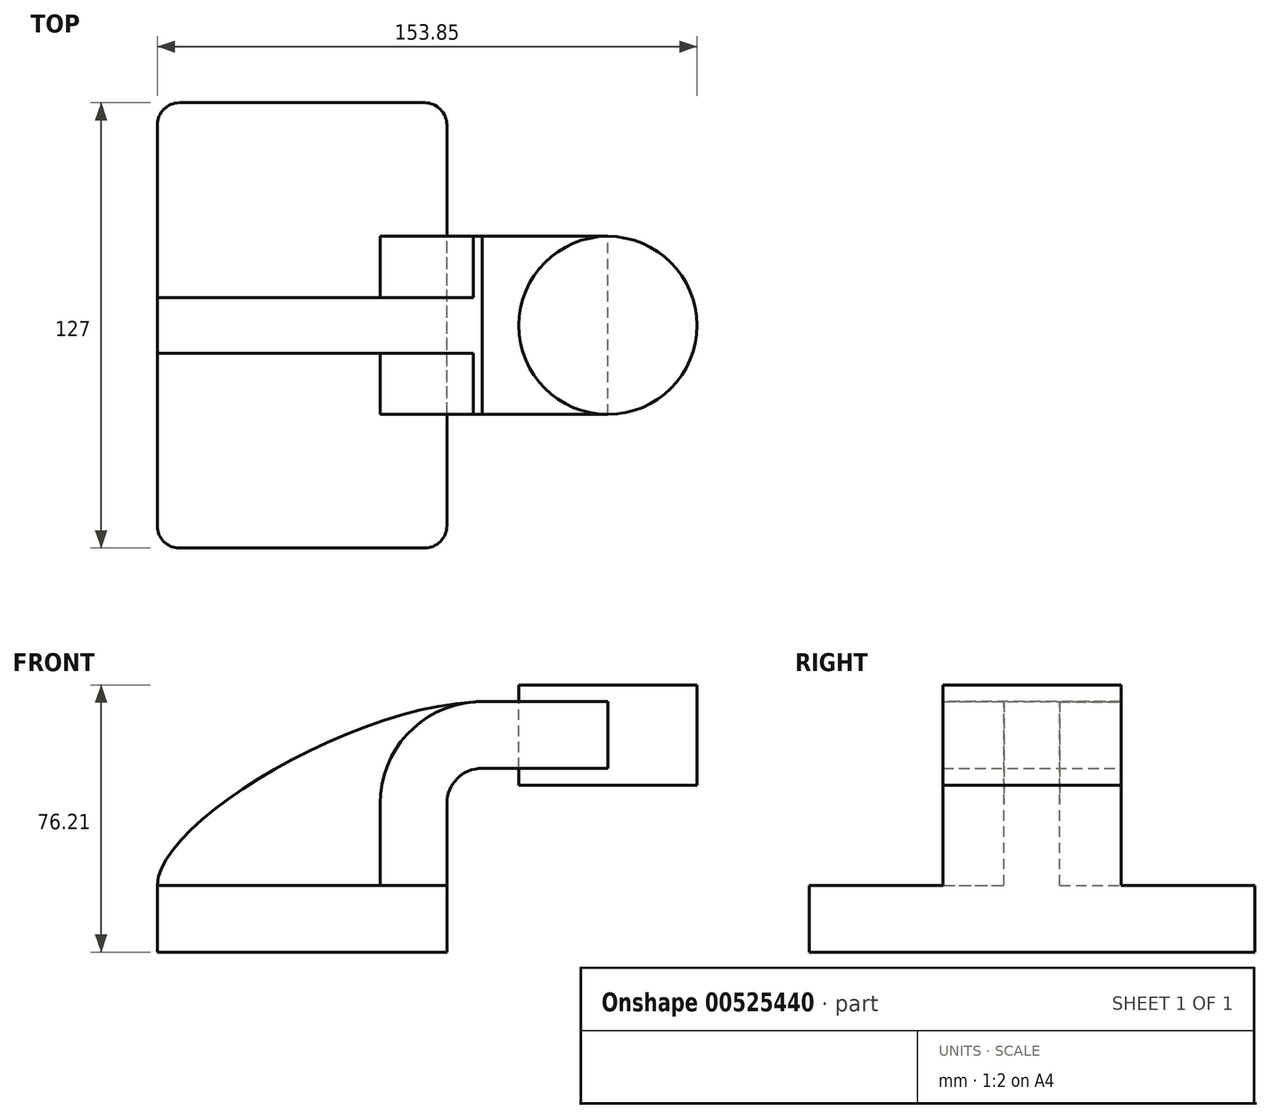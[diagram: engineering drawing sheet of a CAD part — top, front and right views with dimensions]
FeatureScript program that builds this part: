
annotation { "Feature Type Name" : "Feature", "Feature Type Description" : "" }
export const myFeature = defineFeature(function(context is Context, id is Id, definition is map)
    precondition{}
    {
        {
            var Q0;
            Q0=qCreatedBy(makeId("Front.planeOp"),FACE);
            var sketch = newSketch(context, id + "F0", { "sketchPlane" : qUnion([Q0])});
            skLineSegment(sketch, "E0.bottom", {"start": v(-41.28, 9.52) * mm, "end": v(41.27, 9.53) * mm});
            skLineSegment(sketch, "E0.top", {"start": v(-41.28, -9.53) * mm, "end": v(41.28, -9.53) * mm});
            skLineSegment(sketch, "E0.left", {"start": v(-41.28, 9.52) * mm, "end": v(-41.27, -9.53) * mm});
            skLineSegment(sketch, "E0.right", {"start": v(41.28, 9.53) * mm, "end": v(41.28, -9.52) * mm});
            skPoint(sketch, "E0.middle", {"position": v(0, 0) * mm});
            skLineSegment(sketch, "E1.bottom", {"start": v(112.57, 66.68) * mm, "end": v(61.77, 66.68) * mm});
            skLineSegment(sketch, "E1.top", {"start": v(112.57, 38.1) * mm, "end": v(61.77, 38.1) * mm});
            skLineSegment(sketch, "E1.left", {"start": v(112.57, 66.68) * mm, "end": v(112.57, 38.1) * mm});
            skLineSegment(sketch, "E1.right", {"start": v(61.77, 66.67) * mm, "end": v(61.77, 38.1) * mm});
            skPoint(sketch, "E1.middle", {"position": v(87.17, 52.39) * mm});
            skLineSegment(sketch, "E2", {"start": v(41.27, 9.53) * mm, "end": v(41.27, 32.83) * mm});
            skArc(sketch, "E3", {"start": v(41.27, 32.83) * mm, "mid": v(44.22, 39.93) * mm, "end": v(51.32, 42.88) * mm});
            skLineSegment(sketch, "E4", {"start": v(51.32, 42.88) * mm, "end": v(87.17, 42.88) * mm});
            skLineSegment(sketch, "E5.0", {"start": v(51.32, 61.93) * mm, "end": v(87.17, 61.93) * mm});
            skArc(sketch, "E5.1", {"start": v(22.22, 32.83) * mm, "mid": v(30.75, 53.4) * mm, "end": v(51.32, 61.93) * mm});
            skLineSegment(sketch, "E5.2", {"start": v(22.22, 9.53) * mm, "end": v(22.22, 32.83) * mm});
            skLineSegment(sketch, "E6", {"start": v(87.17, 38.1) * mm, "end": v(87.17, 66.68) * mm});
            skFitSpline(sketch, "E7", {"points": [v(-41.28, 9.52) * mm, v(51.32, 61.93) * mm], "startDerivative": vector(0, 52.78) * mm, "endDerivative": vector(111.48, 2.71) * mm});
            skSolve(sketch);
        }
        {
            var Q0;
            Q0=makeQuery(id+"F0.imprint","IMPRINT",FACE,{"disambiguationData":[TD([[makeQuery(id+"F0.imprint","IMPRINT",EDGE,{"derivedFrom":sQuery(id+"F0.wireOp",EDGE,"E0.top")}),1.0]])]});
            extrude(context, id + "F1", {"entities" : qUnion([Q0]), "endBound" : BoundingType.SYMMETRIC, "depth" : 127 * mm, "offsetDistance" : 25.4 * mm});
        }
        {
            var Q0;
            {var subQ1=sQuery(id+"F0.wireOp",EDGE,"E2");Q0=makeQuery(id+"F0.imprint","IMPRINT",FACE,{"disambiguationData":[TD([[makeQuery(id+"F0.imprint","IMPRINT",EDGE,{"derivedFrom":subQ1}),1.0]])]});}
            var Q1;
            {var subQ0=sQuery(id+"F0.wireOp",EDGE,"E5.0");var subQ1=sQuery(id+"F0.wireOp",EDGE,"E1.right");var subQ2=makeQuery(id+"F0.imprint","INTERSECT",VERTEX,{"derivedFrom":[subQ1,subQ0]});Q1=makeQuery(id+"F0.imprint","IMPRINT",FACE,{"disambiguationData":[TD([[makeQuery(id+"F0.imprint","IMPRINT",EDGE,{"disambiguationData":[TD([[subQ2,-1.0]])],"derivedFrom":subQ1}),1.0]])]});}
            extrude(context, id + "F2", {"entities" : qUnion([Q0, Q1]), "operationType" : NewBodyOperationType.ADD, "endBound" : BoundingType.SYMMETRIC, "depth" : 50.8 * mm, "offsetDistance" : 25.4 * mm});
        }
        {
            var Q0;
            {var subQ3=sQuery(id+"F0.wireOp",EDGE,"E5.2");Q0=makeQuery(id+"F0.imprint","IMPRINT",FACE,{"disambiguationData":[TD([[makeQuery(id+"F0.imprint","IMPRINT",EDGE,{"derivedFrom":subQ3}),1.0]])]});}
            extrude(context, id + "F3", {"entities" : qUnion([Q0]), "operationType" : NewBodyOperationType.ADD, "endBound" : BoundingType.SYMMETRIC, "depth" : 15.88 * mm, "offsetDistance" : 25.4 * mm});
        }
        {
            var Q0;
            {var subQ0=sQuery(id+"F0.wireOp",EDGE,"E1.left");Q0=makeQuery(id+"F0.imprint","IMPRINT",FACE,{"disambiguationData":[TD([[makeQuery(id+"F0.imprint","IMPRINT",EDGE,{"derivedFrom":subQ0}),-1.0]])]});}
            var Q1;
            Q1=sQuery(id+"F0.wireOp",EDGE,"E6");
            revolve(context, id + "F4", {"entities" : qUnion([Q0]), "axis" : qUnion([Q1]), "revolveType" : RevolveType.FULL, "oppositeDirection" : true});
        }
        {
            var Q0;
            Q0=makeQuery(id+"F1.opExtrude","CAP_EDGE",EDGE,{"disambiguationData":[OSD([sQuery(id+"F0.wireOp",EDGE,"E0.right")])],"isStart":true});
            var Q1;
            Q1=makeQuery(id+"F1.opExtrude","CAP_EDGE",EDGE,{"disambiguationData":[OSD([sQuery(id+"F0.wireOp",EDGE,"E0.left")])],"isStart":true});
            var Q2;
            Q2=makeQuery(id+"F1.opExtrude","CAP_EDGE",EDGE,{"disambiguationData":[OSD([sQuery(id+"F0.wireOp",EDGE,"E0.left")])],"isStart":false});
            var Q3;
            Q3=makeQuery(id+"F1.opExtrude","CAP_EDGE",EDGE,{"disambiguationData":[OSD([sQuery(id+"F0.wireOp",EDGE,"E0.right")])],"isStart":false});
            fillet(context, id + "F5", {"entities" : qUnion([Q0, Q1, Q2, Q3]), "radius" : 6.35 * mm, "tangentPropagation" : true, "allowEdgeOverflow" : false});
        }
    });
